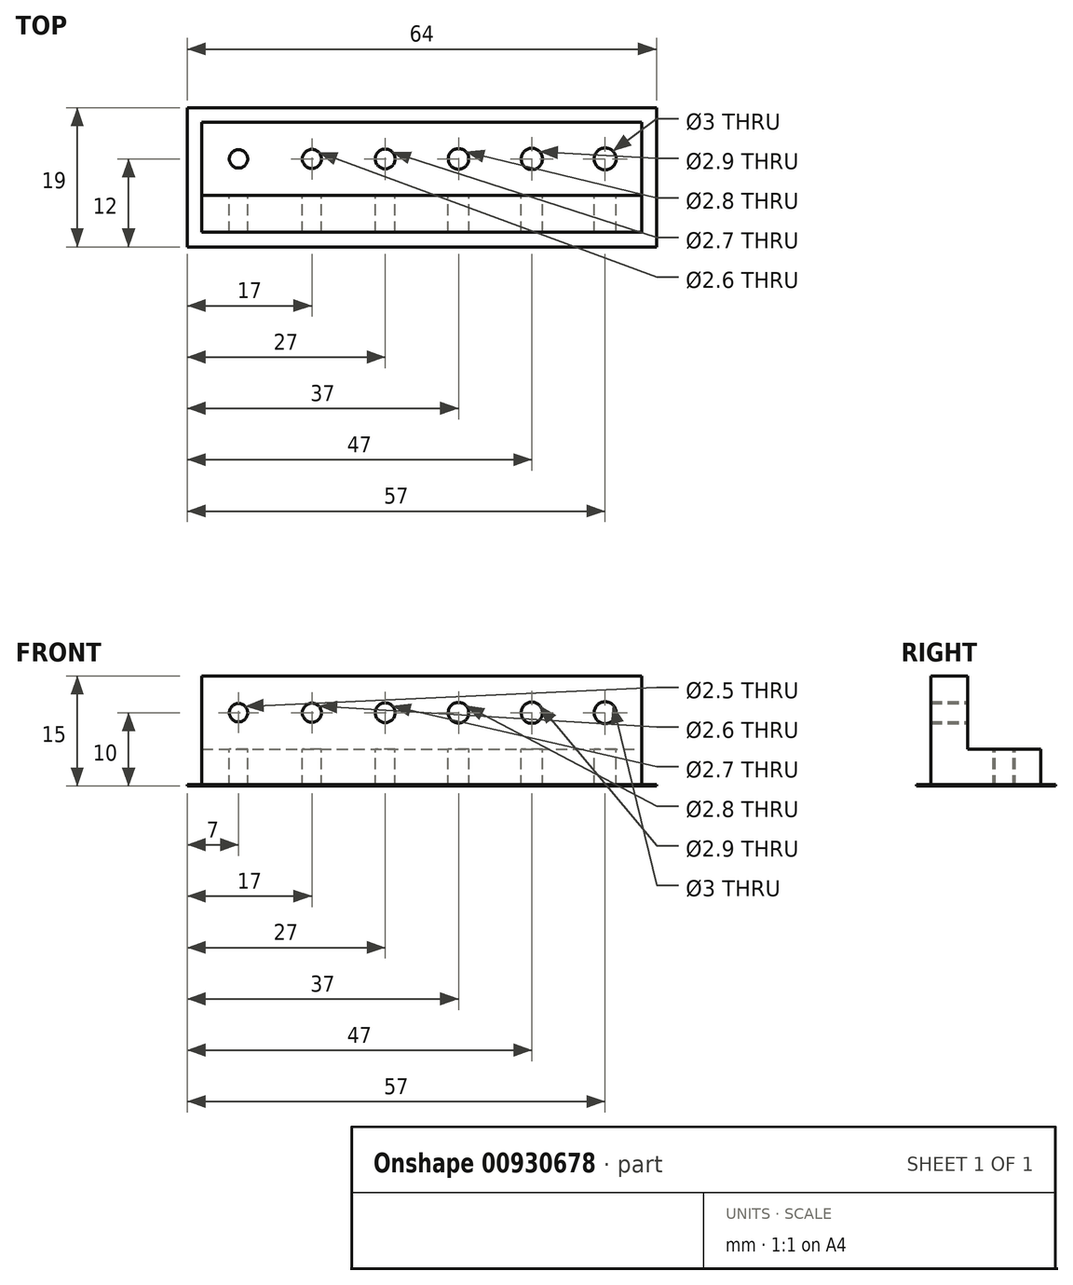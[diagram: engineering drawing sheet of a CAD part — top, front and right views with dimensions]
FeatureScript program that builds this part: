
annotation { "Feature Type Name" : "Feature", "Feature Type Description" : "" }
export const myFeature = defineFeature(function(context is Context, id is Id, definition is map)
    precondition{}
    {
        {
            var Q0;
            Q0=qCreatedBy(makeId("Top.planeOp"),FACE);
            var sketch = newSketch(context, id + "F0", { "sketchPlane" : qUnion([Q0])});
            skLineSegment(sketch, "E0.bottom", {"start": v(0, 0) * mm, "end": v(60, 0) * mm});
            skLineSegment(sketch, "E0.top", {"start": v(0, 15) * mm, "end": v(60, 15) * mm});
            skLineSegment(sketch, "E0.left", {"start": v(0, 0) * mm, "end": v(0, 15) * mm});
            skLineSegment(sketch, "E0.right", {"start": v(60, 0) * mm, "end": v(60, 15) * mm});
            skSolve(sketch);
        }
        {
            var Q0;
            Q0=qSketchRegion(id+"F0",true);
            extrude(context, id + "F1", {"entities" : qUnion([Q0]), "depth" : 5 * mm, "offsetDistance" : 25 * mm});
        }
        {
            var Q0;
            Q0=makeQuery(id+"F1.opExtrude","CAP_FACE",FACE,{"disambiguationData":[OSD([sQuery(id+"F0.wireOp",EDGE,"E0.bottom"),sQuery(id+"F0.wireOp",EDGE,"E0.top"),sQuery(id+"F0.wireOp",EDGE,"E0.left"),sQuery(id+"F0.wireOp",EDGE,"E0.right")])],"isStart":false});
            var sketch = newSketch(context, id + "F2", { "sketchPlane" : qUnion([Q0])});
            skLineSegment(sketch, "E1.bottom", {"start": v(0, 0) * mm, "end": v(60, 0) * mm});
            skLineSegment(sketch, "E1.top", {"start": v(0, 5) * mm, "end": v(60, 5) * mm});
            skLineSegment(sketch, "E1.left", {"start": v(0, 0) * mm, "end": v(0, 5) * mm});
            skLineSegment(sketch, "E1.right", {"start": v(60, 0) * mm, "end": v(60, 5) * mm});
            skSolve(sketch);
        }
        {
            var Q0;
            Q0=qSketchRegion(id+"F2",true);
            extrude(context, id + "F3", {"entities" : qUnion([Q0]), "operationType" : NewBodyOperationType.ADD, "depth" : 10 * mm, "offsetDistance" : 25 * mm});
        }
        {
            var Q0;
            Q0=makeQuery(id+"F1.opExtrude","CAP_FACE",FACE,{"disambiguationData":[OSD([sQuery(id+"F0.wireOp",EDGE,"E0.bottom"),sQuery(id+"F0.wireOp",EDGE,"E0.top"),sQuery(id+"F0.wireOp",EDGE,"E0.left"),sQuery(id+"F0.wireOp",EDGE,"E0.right")])],"isStart":false});
            var sketch = newSketch(context, id + "F4", { "sketchPlane" : qUnion([Q0])});
            skLineSegment(sketch, "E2", {"start": v(0, 10) * mm, "end": v(60, 10) * mm, "construction": true});
            skLineSegment(sketch, "E3", {"start": v(5, 15) * mm, "end": v(5, 5) * mm, "construction": true});
            skLineSegment(sketch, "E4", {"start": v(15, 15) * mm, "end": v(15, 5) * mm, "construction": true});
            skLineSegment(sketch, "E5", {"start": v(25, 15) * mm, "end": v(25, 5) * mm, "construction": true});
            skLineSegment(sketch, "E6", {"start": v(35, 15) * mm, "end": v(35, 5) * mm, "construction": true});
            skLineSegment(sketch, "E7", {"start": v(45, 15) * mm, "end": v(45, 5) * mm, "construction": true});
            skLineSegment(sketch, "E8", {"start": v(55, 15) * mm, "end": v(55, 5) * mm, "construction": true});
            skCircle(sketch, "E9", {"center": v(5, 10) * mm, "radius": 1.25 * mm});
            skCircle(sketch, "E10", {"center": v(15, 10) * mm, "radius": 1.3 * mm});
            skCircle(sketch, "E11", {"center": v(25, 10) * mm, "radius": 1.35 * mm});
            skCircle(sketch, "E12", {"center": v(35, 10) * mm, "radius": 1.4 * mm});
            skCircle(sketch, "E13", {"center": v(45, 10) * mm, "radius": 1.45 * mm});
            skCircle(sketch, "E14", {"center": v(55, 10) * mm, "radius": 1.5 * mm});
            skSolve(sketch);
        }
        {
            var Q0;
            Q0=qSketchRegion(id+"F4",true);
            extrude(context, id + "F5", {"entities" : qUnion([Q0]), "operationType" : NewBodyOperationType.REMOVE, "endBound" : BoundingType.UP_TO_NEXT, "oppositeDirection" : true, "depth" : 2.5 * mm, "offsetDistance" : 25 * mm});
        }
        {
            var Q0;
            Q0=makeQuery(id+"F3.opExtrude","SWEPT_FACE",FACE,{"disambiguationData":[OSD([sQuery(id+"F2.wireOp",EDGE,"E1.top")])]});
            var sketch = newSketch(context, id + "F6", { "sketchPlane" : qUnion([Q0])});
            skLineSegment(sketch, "E15", {"start": v(-60, 10) * mm, "end": v(0, 10) * mm, "construction": true});
            skLineSegment(sketch, "E16", {"start": v(-55, 15) * mm, "end": v(-55, 5) * mm, "construction": true});
            skLineSegment(sketch, "E17", {"start": v(-45, 15) * mm, "end": v(-45, 5) * mm, "construction": true});
            skLineSegment(sketch, "E18", {"start": v(-35, 15) * mm, "end": v(-35, 5) * mm, "construction": true});
            skLineSegment(sketch, "E19", {"start": v(-25, 15) * mm, "end": v(-25, 5) * mm, "construction": true});
            skLineSegment(sketch, "E20", {"start": v(-15, 15) * mm, "end": v(-15, 5) * mm, "construction": true});
            skLineSegment(sketch, "E21", {"start": v(-5, 15) * mm, "end": v(-5, 5) * mm, "construction": true});
            skCircle(sketch, "E22", {"center": v(-55, 10) * mm, "radius": 1.5 * mm});
            skCircle(sketch, "E23", {"center": v(-45, 10) * mm, "radius": 1.45 * mm});
            skCircle(sketch, "E24", {"center": v(-35, 10) * mm, "radius": 1.4 * mm});
            skCircle(sketch, "E25", {"center": v(-25, 10) * mm, "radius": 1.35 * mm});
            skCircle(sketch, "E26", {"center": v(-15, 10) * mm, "radius": 1.3 * mm});
            skCircle(sketch, "E27", {"center": v(-5, 10) * mm, "radius": 1.25 * mm});
            skSolve(sketch);
        }
        {
            var Q0;
            Q0=qSketchRegion(id+"F6",true);
            extrude(context, id + "F7", {"entities" : qUnion([Q0]), "operationType" : NewBodyOperationType.REMOVE, "endBound" : BoundingType.UP_TO_NEXT, "oppositeDirection" : true, "depth" : 2.5 * mm, "offsetDistance" : 25 * mm});
        }
        {
            var Q0;
            Q0=qCreatedBy(makeId("Top.planeOp"),FACE);
            var sketch = newSketch(context, id + "F8", { "sketchPlane" : qUnion([Q0])});
            skLineSegment(sketch, "E28", {"start": v(0, 0) * mm, "end": v(0, 15) * mm});
            skLineSegment(sketch, "E29", {"start": v(0, 15) * mm, "end": v(60, 15) * mm});
            skLineSegment(sketch, "E30", {"start": v(60, 15) * mm, "end": v(60, 0) * mm});
            skLineSegment(sketch, "E31", {"start": v(60, 0) * mm, "end": v(0, 0) * mm});
            skLineSegment(sketch, "E32.bottom", {"start": v(-2, 17) * mm, "end": v(62, 17) * mm});
            skLineSegment(sketch, "E32.top", {"start": v(-2, -2) * mm, "end": v(62, -2) * mm});
            skLineSegment(sketch, "E32.left", {"start": v(-2, 17) * mm, "end": v(-2, -2) * mm});
            skLineSegment(sketch, "E32.right", {"start": v(62, 17) * mm, "end": v(62, -2) * mm});
            skSolve(sketch);
        }
        {
            var Q0;
            Q0=qSketchRegion(id+"F8",true);
            extrude(context, id + "F9", {"entities" : qUnion([Q0]), "operationType" : NewBodyOperationType.ADD, "depth" : 0.2 * mm, "offsetDistance" : 25 * mm});
        }
    });
